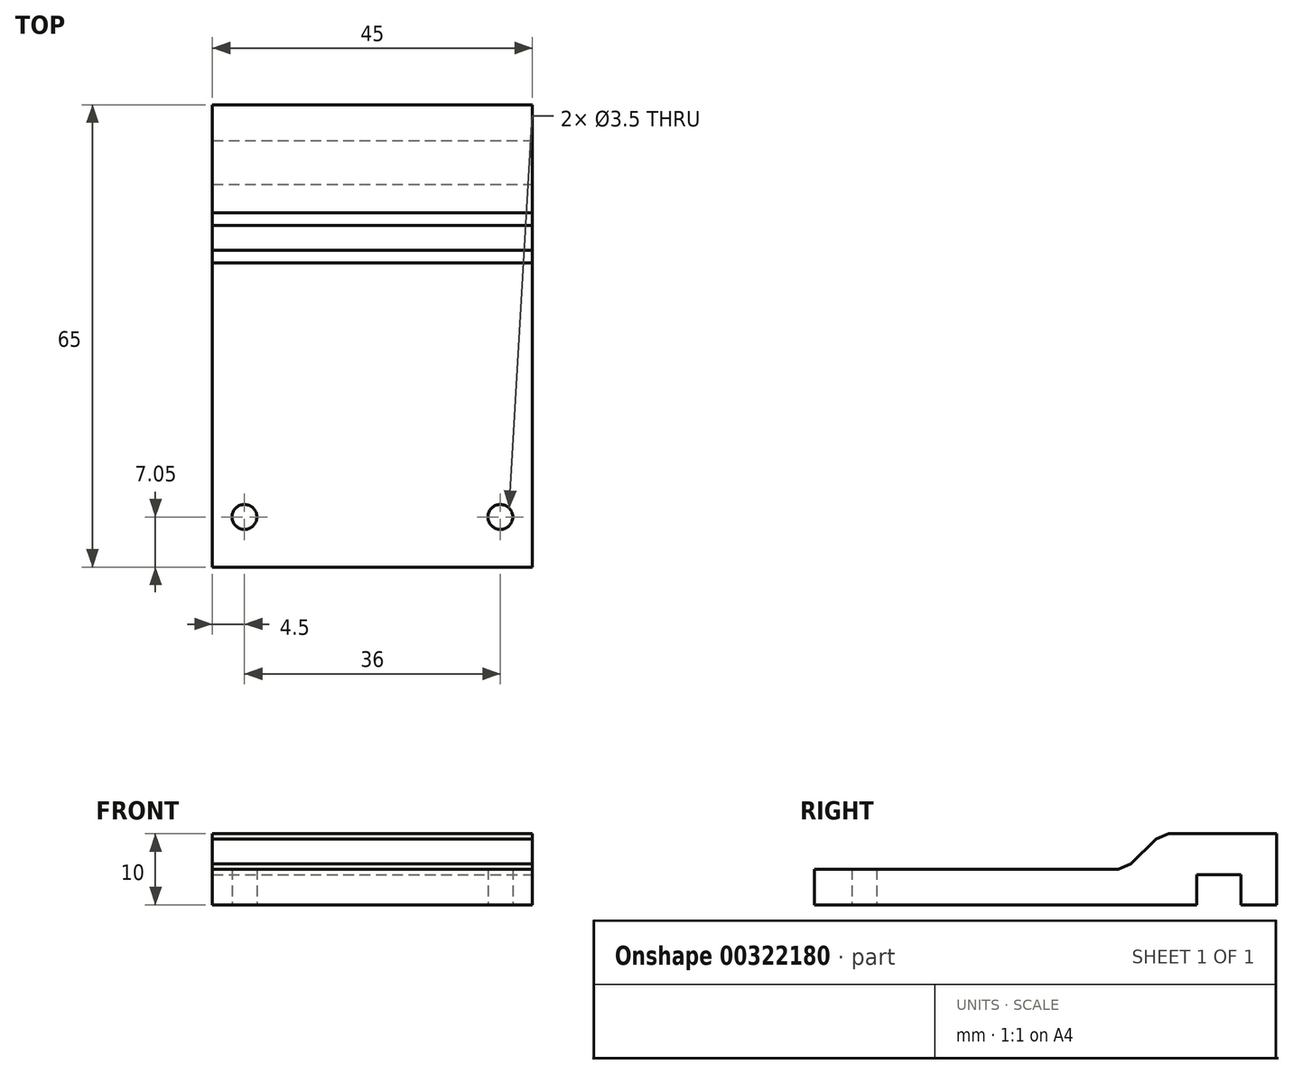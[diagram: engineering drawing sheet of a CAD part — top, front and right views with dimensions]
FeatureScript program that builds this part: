
annotation { "Feature Type Name" : "Feature", "Feature Type Description" : "" }
export const myFeature = defineFeature(function(context is Context, id is Id, definition is map)
    precondition{}
    {
        {
            assignVariable(context, id + "F0", {"name" : "hoehe_gesamt", "anyValue" : 10});
        }
        {
            var Q0;
            Q0=qCreatedBy(makeId("Top.planeOp"),FACE);
            var sketch = newSketch(context, id + "F1", { "sketchPlane" : qUnion([Q0])});
            skLineSegment(sketch, "E0.bottom", {"start": v(22.5, -32.5) * mm, "end": v(-22.5, -32.5) * mm});
            skLineSegment(sketch, "E0.top", {"start": v(22.5, 32.5) * mm, "end": v(-22.5, 32.5) * mm});
            skLineSegment(sketch, "E0.left", {"start": v(22.5, -32.5) * mm, "end": v(22.5, 32.5) * mm});
            skLineSegment(sketch, "E0.right", {"start": v(-22.5, -32.5) * mm, "end": v(-22.5, 32.5) * mm});
            skPoint(sketch, "E0.middle", {"position": v(0, 0) * mm});
            skLineSegment(sketch, "E1.bottom", {"start": v(-22.5, 27.5) * mm, "end": v(22.5, 27.5) * mm});
            skLineSegment(sketch, "E1.top", {"start": v(-22.5, 21.3) * mm, "end": v(22.5, 21.3) * mm});
            skLineSegment(sketch, "E1.left", {"start": v(-22.5, 27.5) * mm, "end": v(-22.5, 21.3) * mm});
            skLineSegment(sketch, "E1.right", {"start": v(22.5, 27.5) * mm, "end": v(22.5, 21.3) * mm});
            skCircle(sketch, "E2", {"center": v(-18, -25.45) * mm, "radius": 1.75 * mm});
            skCircle(sketch, "E3", {"center": v(18, -25.45) * mm, "radius": 1.75 * mm});
            skLineSegment(sketch, "E4", {"start": v(-18, -25.45) * mm, "end": v(18, -25.45) * mm, "construction": true});
            skPoint(sketch, "E5", {"position": v(0, -25.45) * mm});
            skSolve(sketch);
        }
        {
            var Q0;
            {var subQ0=sQuery(id+"F1.wireOp",EDGE,"E0.top");Q0=makeQuery(id+"F1.imprint","IMPRINT",FACE,{"disambiguationData":[TD([[makeQuery(id+"F1.imprint","IMPRINT",EDGE,{"derivedFrom":subQ0}),1.0]])]});}
            var Q1;
            Q1=makeQuery(id+"F1.imprint","IMPRINT",FACE,{"disambiguationData":[TD([[makeQuery(id+"F1.imprint","IMPRINT",EDGE,{"derivedFrom":sQuery(id+"F1.wireOp",EDGE,"E1.bottom")}),-1.0]])]});
            var Q2;
            {var subQ1=sQuery(id+"F1.wireOp",EDGE,"E0.bottom");Q2=makeQuery(id+"F1.imprint","IMPRINT",FACE,{"disambiguationData":[TD([[makeQuery(id+"F1.imprint","IMPRINT",EDGE,{"derivedFrom":subQ1}),-1.0]])]});}
            extrude(context, id + "F2", {"entities" : qUnion([Q0, Q1, Q2]), "depth" : (getVariable(context, 'hoehe_gesamt')) * mm});
        }
        {
            var Q0;
            Q0=makeQuery(id+"F1.imprint","IMPRINT",FACE,{"disambiguationData":[TD([[makeQuery(id+"F1.imprint","IMPRINT",EDGE,{"derivedFrom":sQuery(id+"F1.wireOp",EDGE,"E1.bottom")}),-1.0]])]});
            extrude(context, id + "F3", {"entities" : qUnion([Q0]), "operationType" : NewBodyOperationType.REMOVE, "depth" : 4.22 * mm});
        }
        {
            var Q0;
            Q0=makeQuery(id+"F2.opExtrude","CAP_FACE",FACE,{"disambiguationData":[OSD([sQuery(id+"F1.wireOp",EDGE,"E0.bottom"),sQuery(id+"F1.wireOp",EDGE,"E0.top"),sQuery(id+"F1.wireOp",EDGE,"E0.left"),sQuery(id+"F1.wireOp",EDGE,"E0.right"),sQuery(id+"F1.wireOp",EDGE,"E1.left"),sQuery(id+"F1.wireOp",EDGE,"E1.right"),sQuery(id+"F1.wireOp",EDGE,"E2"),sQuery(id+"F1.wireOp",EDGE,"E3")])],"isStart":false});
            var sketch = newSketch(context, id + "F4", { "sketchPlane" : qUnion([Q0])});
            skLineSegment(sketch, "E6.bottom", {"start": v(-22.5, -32.5) * mm, "end": v(22.5, -32.5) * mm});
            skLineSegment(sketch, "E6.top", {"start": v(-22.5, 16.3) * mm, "end": v(22.5, 16.3) * mm});
            skLineSegment(sketch, "E6.left", {"start": v(-22.5, -32.5) * mm, "end": v(-22.5, 16.3) * mm});
            skLineSegment(sketch, "E6.right", {"start": v(22.5, -32.5) * mm, "end": v(22.5, 16.3) * mm});
            skSolve(sketch);
        }
        {
            var Q0;
            Q0=makeQuery(id+"F4.imprint","IMPRINT",FACE,{"disambiguationData":[TD([[makeQuery(id+"F4.imprint","IMPRINT",EDGE,{"derivedFrom":sQuery(id+"F4.wireOp",EDGE,"E6.bottom")}),-1.0]])]});
            extrude(context, id + "F5", {"entities" : qUnion([Q0]), "operationType" : NewBodyOperationType.REMOVE, "oppositeDirection" : true, "depth" : (getVariable(context, 'hoehe_gesamt') / 2) * mm});
        }
        {
            var Q0;
            Q0=makeQuery(id+"F5.boolean.opBoolean","COPY",EDGE,{"derivedFrom":makeQuery(id+"F5.opExtrude","CAP_EDGE",EDGE,{"disambiguationData":[OSD([sQuery(id+"F4.wireOp",EDGE,"E6.top")])],"isStart":false})});
            chamfer(context, id + "F6", {"entities" : qUnion([Q0]), "width" : 5 * mm, "tangentPropagation" : true});
        }
        {
            var Q0;
            {var subQ0=sQuery(id+"F4.wireOp",EDGE,"E6.top");Q0=makeQuery(id+"F6.opChamfer","BLEND_EDGE",EDGE,{"blendedFrom":[makeQuery(id+"F5.boolean.opBoolean","COPY",EDGE,{"derivedFrom":makeQuery(id+"F5.opExtrude","CAP_EDGE",EDGE,{"disambiguationData":[OSD([subQ0])],"isStart":false})}),makeQuery(id+"F5.boolean.opBoolean","COPY",FACE,{"derivedFrom":makeQuery(id+"F5.opExtrude","CAP_FACE",FACE,{"disambiguationData":[OSD([sQuery(id+"F1.wireOp",EDGE,"E2"),sQuery(id+"F1.wireOp",EDGE,"E3"),sQuery(id+"F4.wireOp",EDGE,"E6.bottom"),subQ0,sQuery(id+"F4.wireOp",EDGE,"E6.left"),sQuery(id+"F4.wireOp",EDGE,"E6.right")])],"isStart":false})})],"blendedInto":[makeQuery(id+"F5.boolean.opBoolean","COPY",FACE,{"derivedFrom":makeQuery(id+"F5.opExtrude","CAP_FACE",FACE,{"disambiguationData":[OSD([sQuery(id+"F1.wireOp",EDGE,"E2"),sQuery(id+"F1.wireOp",EDGE,"E3"),sQuery(id+"F4.wireOp",EDGE,"E6.bottom"),subQ0,sQuery(id+"F4.wireOp",EDGE,"E6.left"),sQuery(id+"F4.wireOp",EDGE,"E6.right")])],"isStart":false})})]});}
            chamfer(context, id + "F7", {"entities" : qUnion([Q0]), "width" : 2.5 * mm, "tangentPropagation" : true});
        }
        {
            var Q0;
            Q0=makeQuery(id+"F6.opChamfer","BLEND_EDGE",EDGE,{"blendedFrom":[makeQuery(id+"F5.boolean.opBoolean","COPY",EDGE,{"derivedFrom":makeQuery(id+"F5.opExtrude","CAP_EDGE",EDGE,{"disambiguationData":[OSD([sQuery(id+"F4.wireOp",EDGE,"E6.top")])],"isStart":false})}),makeQuery(id+"F2.opExtrude","CAP_FACE",FACE,{"disambiguationData":[OSD([sQuery(id+"F1.wireOp",EDGE,"E0.bottom"),sQuery(id+"F1.wireOp",EDGE,"E0.top"),sQuery(id+"F1.wireOp",EDGE,"E0.left"),sQuery(id+"F1.wireOp",EDGE,"E0.right"),sQuery(id+"F1.wireOp",EDGE,"E1.left"),sQuery(id+"F1.wireOp",EDGE,"E1.right"),sQuery(id+"F1.wireOp",EDGE,"E2"),sQuery(id+"F1.wireOp",EDGE,"E3")])],"isStart":false})],"blendedInto":[makeQuery(id+"F2.opExtrude","CAP_FACE",FACE,{"disambiguationData":[OSD([sQuery(id+"F1.wireOp",EDGE,"E0.bottom"),sQuery(id+"F1.wireOp",EDGE,"E0.top"),sQuery(id+"F1.wireOp",EDGE,"E0.left"),sQuery(id+"F1.wireOp",EDGE,"E0.right"),sQuery(id+"F1.wireOp",EDGE,"E1.left"),sQuery(id+"F1.wireOp",EDGE,"E1.right"),sQuery(id+"F1.wireOp",EDGE,"E2"),sQuery(id+"F1.wireOp",EDGE,"E3")])],"isStart":false})]});
            chamfer(context, id + "F8", {"entities" : qUnion([Q0]), "width" : 2.5 * mm, "tangentPropagation" : true});
        }
    });
